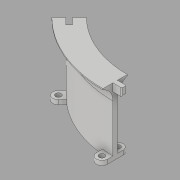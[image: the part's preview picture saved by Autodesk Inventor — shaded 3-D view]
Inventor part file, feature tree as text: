
AUTODESK INVENTOR PART (.ipt)
format: ipt  version: 2017 (Build 210142000, 142)  size: 215,552 bytes
history: native  units: in
note: dims shown in document units (in); Inventor stores cm internally (conversion verified against a paired STEP export)
features: extrude x5, sketch x5, fillet x2, projected_geometry x1
ambient origin geometry x8: Origin, YZ Plane, XZ Plane, XY Plane, X Axis, Y Axis, Z Axis, Center Point
bodies: Solid1 (feature_tree)
feature tree (13):
  extrude  "Extrusion1"  TaperAngle=45.0deg  [1 undecoded]
  extrude  "Extrusion2"  Depth=0.05in TaperAngle=0.0deg
  fillet  "Fillet1"  Radius=0.2in
  extrude  "Extrusion3"  Depth=0.45in
  extrude  "Extrusion4"  Depth=0.7in
  extrude  "Extrusion5"  Depth=0.05in
  fillet  "Fillet2"  Radius=0.25in
  sketch  "Sketch1"  dims[d0=1.1in d1=45.0deg]
  sketch  "Sketch2"  dims[d2=5.0in d3=0.05in d4=0.0in d5=0.2in]
  projected_geometry  "Projected Loop1"
  sketch  "Sketch3"  dims[d6=0.45in d7=0.45in]
  sketch  "Sketch4"  dims[d8=3.0in d9=0.0in d10=0.7in]
  sketch  "Sketch5"  dims[d11=0.25in d12=0.5in d13=0.25in d14=0.5in d15=0.2in d16=0.0in d17=0.45in d18=0.45in d19=0.35in d20=0.4in d21=0.0in d22=0.445in d23=0.445in d24=0.35in d25=0.4in d26=0.0in d27=0.05in]
note: 1 required parameter value undecoded (feature->parameter linkage not recoverable at this tier; creation-order binding heuristic only, values carry confidence <= 0.55)
